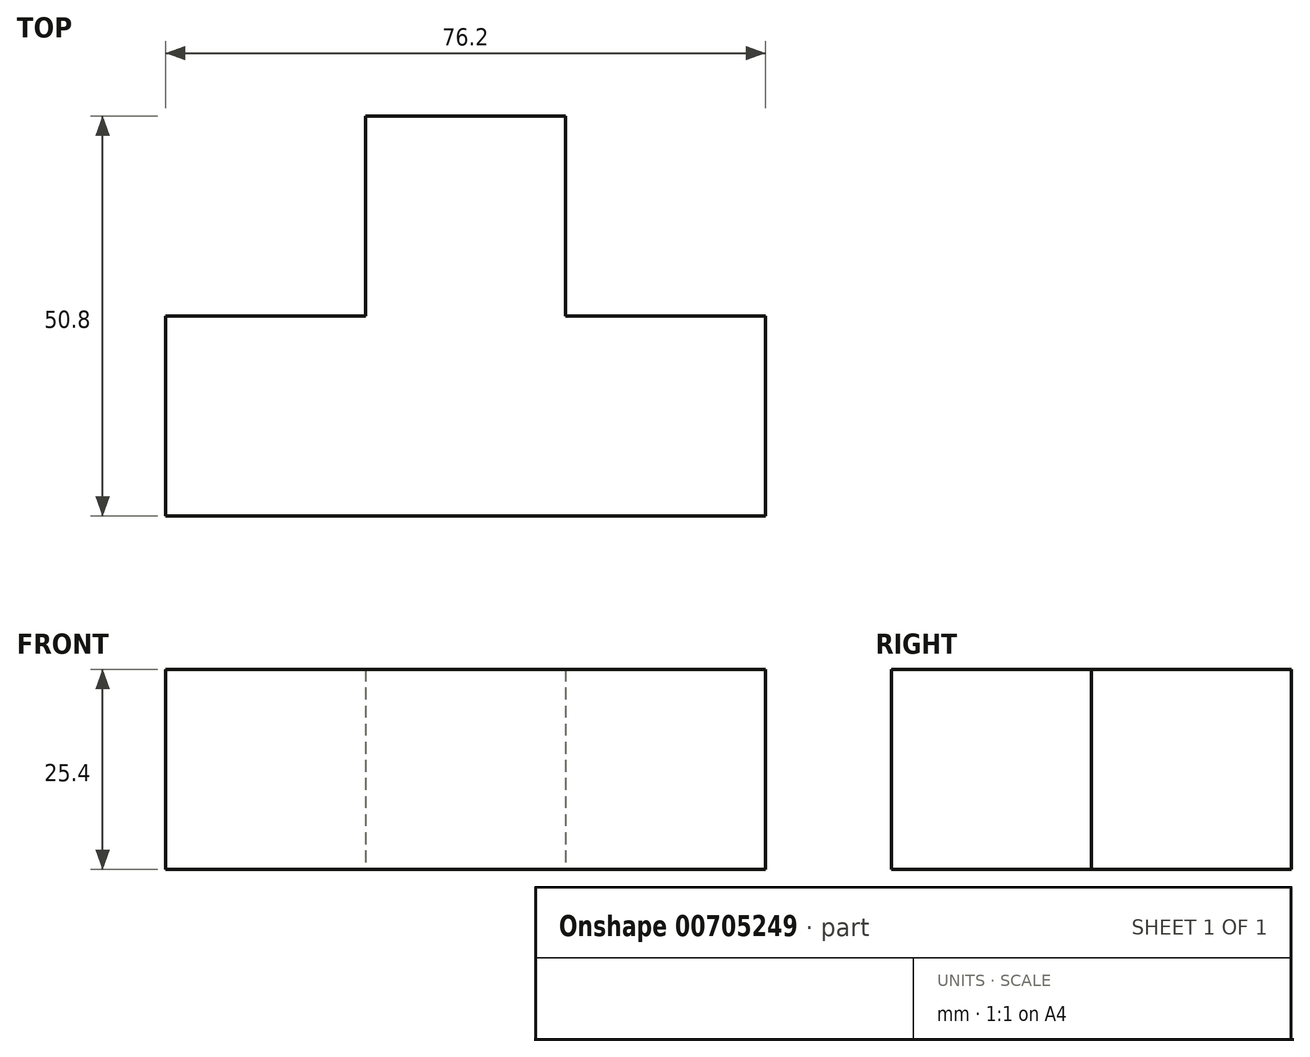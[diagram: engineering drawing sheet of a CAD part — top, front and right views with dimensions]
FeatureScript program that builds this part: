
annotation { "Feature Type Name" : "Feature", "Feature Type Description" : "" }
export const myFeature = defineFeature(function(context is Context, id is Id, definition is map)
    precondition{}
    {
        {
            var Q0;
            Q0=qCreatedBy(makeId("Front.planeOp"),FACE);
            var sketch = newSketch(context, id + "F0", { "sketchPlane" : qUnion([Q0])});
            skLineSegment(sketch, "E0.bottom", {"start": v(0, 0) * mm, "end": v(25.4, 0) * mm});
            skLineSegment(sketch, "E0.top", {"start": v(0, 25.4) * mm, "end": v(25.4, 25.4) * mm});
            skLineSegment(sketch, "E0.left", {"start": v(0, 0) * mm, "end": v(0, 25.4) * mm});
            skLineSegment(sketch, "E0.right", {"start": v(25.4, 0) * mm, "end": v(25.4, 25.4) * mm});
            skPoint(sketch, "E1.oppositeSnap0", {"position": v(12.7, 0) * mm});
            skLineSegment(sketch, "E1.bottom", {"start": v(0, 25.4) * mm, "end": v(-25.4, 25.4) * mm});
            skLineSegment(sketch, "E1.top", {"start": v(0, 0) * mm, "end": v(-25.4, 0) * mm});
            skLineSegment(sketch, "E1.left", {"start": v(0, 25.4) * mm, "end": v(0, 0) * mm});
            skLineSegment(sketch, "E1.right", {"start": v(-25.4, 25.4) * mm, "end": v(-25.4, 0) * mm});
            skLineSegment(sketch, "E2.bottom", {"start": v(-25.4, 25.4) * mm, "end": v(-50.8, 25.4) * mm});
            skLineSegment(sketch, "E2.top", {"start": v(-25.4, 0) * mm, "end": v(-50.8, 0) * mm});
            skLineSegment(sketch, "E2.right", {"start": v(-50.8, 25.4) * mm, "end": v(-50.8, 0) * mm});
            skLineSegment(sketch, "E3.bottom", {"start": v(-50.8, 25.4) * mm, "end": v(-25.4, 25.4) * mm});
            skLineSegment(sketch, "E3.top", {"start": v(-50.8, 50.8) * mm, "end": v(-25.4, 50.8) * mm});
            skLineSegment(sketch, "E3.left", {"start": v(-50.8, 25.4) * mm, "end": v(-50.8, 50.8) * mm});
            skLineSegment(sketch, "E3.right", {"start": v(-25.4, 25.4) * mm, "end": v(-25.4, 50.8) * mm});
            skSolve(sketch);
        }
        {
            var Q0;
            Q0=makeQuery(id+"F0.imprint","IMPRINT",FACE,{"disambiguationData":[TD([[makeQuery(id+"F0.imprint","IMPRINT",EDGE,{"derivedFrom":sQuery(id+"F0.wireOp",EDGE,"E2.top")}),-1.0]])]});
            var Q1;
            Q1=makeQuery(id+"F0.imprint","IMPRINT",FACE,{"disambiguationData":[TD([[makeQuery(id+"F0.imprint","IMPRINT",EDGE,{"derivedFrom":sQuery(id+"F0.wireOp",EDGE,"E1.bottom")}),1.0]])]});
            var Q2;
            Q2=makeQuery(id+"F0.imprint","IMPRINT",FACE,{"disambiguationData":[TD([[makeQuery(id+"F0.imprint","IMPRINT",EDGE,{"derivedFrom":sQuery(id+"F0.wireOp",EDGE,"E0.bottom")}),1.0]])]});
            var Q3;
            Q3=makeQuery(id+"F0.imprint","IMPRINT",FACE,{"disambiguationData":[TD([[makeQuery(id+"F0.imprint","IMPRINT",EDGE,{"derivedFrom":sQuery(id+"F0.wireOp",EDGE,"E3.bottom")}),1.0]])]});
            extrude(context, id + "F1", {"entities" : qUnion([Q0, Q1, Q2, Q3]), "depth" : 25.4 * mm, "offsetDistance" : 25.4 * mm});
        }
        {
            var Q0;
            Q0=qCreatedBy(makeId("Top.planeOp"),FACE);
            var sketch = newSketch(context, id + "F2", { "sketchPlane" : qUnion([Q0])});
            skLineSegment(sketch, "E4.bottom", {"start": v(0, 0) * mm, "end": v(-25.4, 0) * mm});
            skLineSegment(sketch, "E4.top", {"start": v(0, 25.4) * mm, "end": v(-25.4, 25.4) * mm});
            skLineSegment(sketch, "E4.left", {"start": v(0, 0) * mm, "end": v(0, 25.4) * mm});
            skLineSegment(sketch, "E4.right", {"start": v(-25.4, 0) * mm, "end": v(-25.4, 25.4) * mm});
            skSolve(sketch);
        }
        {
            var Q0;
            Q0 = qSketchRegion(id + "F2", true);
            extrude(context, id + "F3", {"entities" : qUnion([Q0]), "operationType" : NewBodyOperationType.ADD, "depth" : 25.4 * mm, "offsetDistance" : 25.4 * mm});
        }
    });
